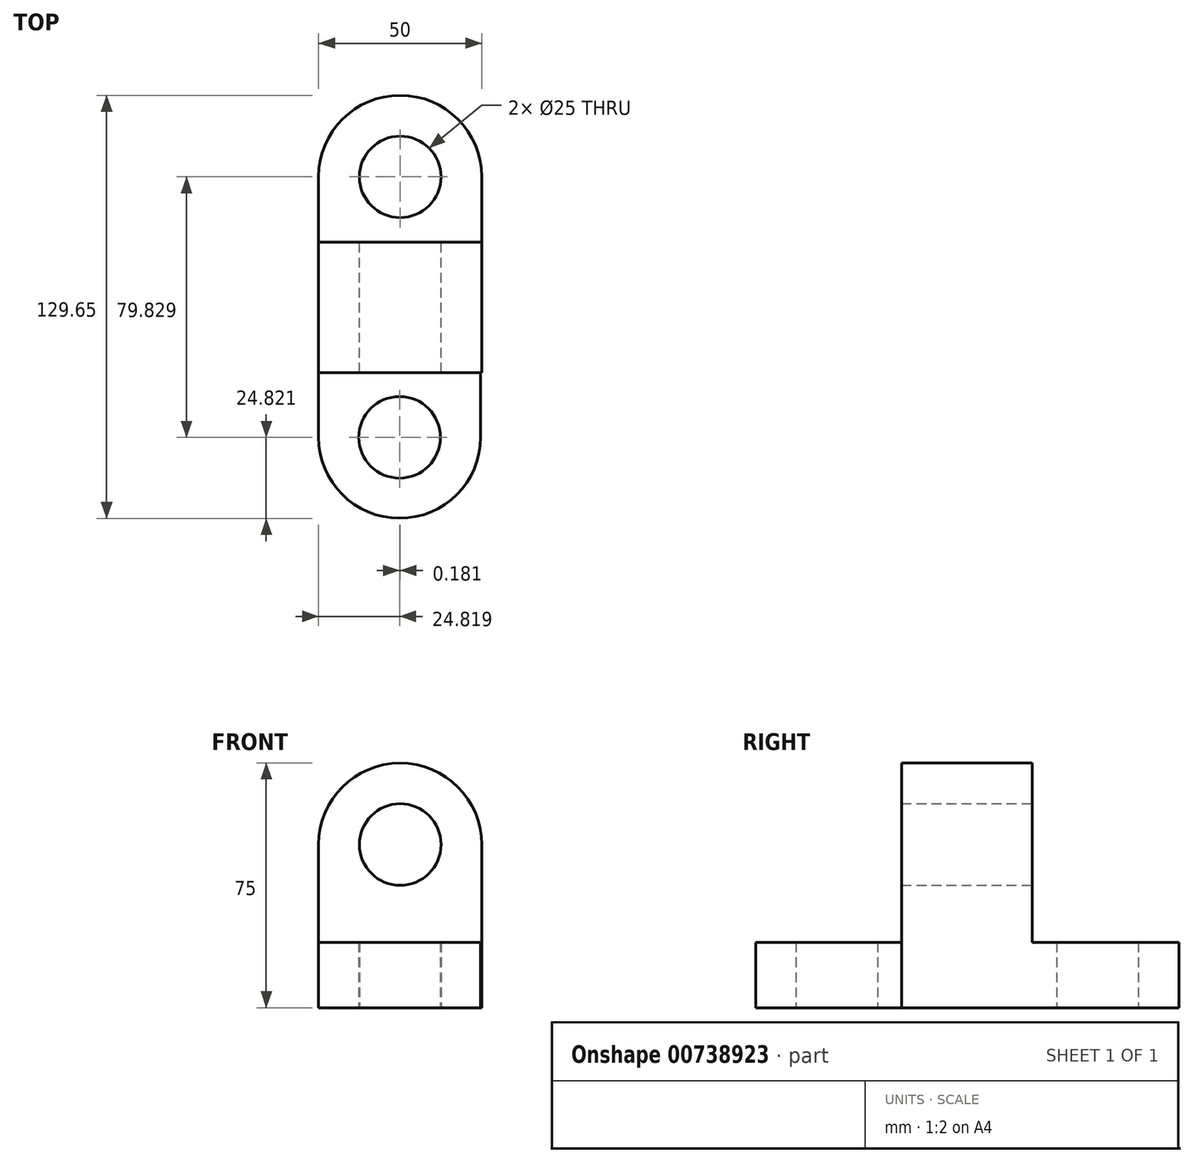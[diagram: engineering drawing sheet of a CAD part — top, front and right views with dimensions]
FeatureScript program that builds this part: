
annotation { "Feature Type Name" : "Feature", "Feature Type Description" : "" }
export const myFeature = defineFeature(function(context is Context, id is Id, definition is map)
    precondition{}
    {
        {
            var Q0;
            Q0=qCreatedBy(makeId("Front.planeOp"),FACE);
            var sketch = newSketch(context, id + "F0", { "sketchPlane" : qUnion([Q0])});
            skLineSegment(sketch, "E0.bottom", {"start": v(0, 0) * mm, "end": v(50, 0) * mm});
            skLineSegment(sketch, "E0.top", {"start": v(0, 50) * mm, "end": v(50, 50) * mm});
            skLineSegment(sketch, "E0.left", {"start": v(0, 0) * mm, "end": v(0, 50) * mm});
            skLineSegment(sketch, "E0.right", {"start": v(50, 0) * mm, "end": v(50, 50) * mm});
            skArc(sketch, "E1", {"start": v(50, 50) * mm, "mid": v(25, 75) * mm, "end": v(0, 50) * mm});
            skCircle(sketch, "E2", {"center": v(25, 50) * mm, "radius": 12.5 * mm});
            skSolve(sketch);
        }
        {
            var Q0;
            Q0 = qSketchRegion(id + "F0", true);
            extrude(context, id + "F1", {"entities" : qUnion([Q0]), "depth" : 40 * mm, "offsetDistance" : 25 * mm});
        }
        {
            var Q0;
            Q0=qCreatedBy(makeId("Top.planeOp"),FACE);
            var sketch = newSketch(context, id + "F2", { "sketchPlane" : qUnion([Q0])});
            skLineSegment(sketch, "E3.bottom", {"start": v(0, 0) * mm, "end": v(50, 0) * mm});
            skLineSegment(sketch, "E3.top", {"start": v(0, 20) * mm, "end": v(50, 20) * mm});
            skLineSegment(sketch, "E3.left", {"start": v(0, 0) * mm, "end": v(0, 20) * mm});
            skLineSegment(sketch, "E3.right", {"start": v(50, 0) * mm, "end": v(50, 20) * mm});
            skArc(sketch, "E4", {"start": v(50, 20) * mm, "mid": v(25, 45) * mm, "end": v(0, 20) * mm});
            skCircle(sketch, "E5", {"center": v(25, 20) * mm, "radius": 12.5 * mm});
            skSolve(sketch);
        }
        {
            var Q0;
            Q0 = qSketchRegion(id + "F2", true);
            extrude(context, id + "F3", {"entities" : qUnion([Q0]), "operationType" : NewBodyOperationType.ADD, "depth" : 20 * mm, "offsetDistance" : 25 * mm});
        }
        {
            var Q0;
            Q0=qCreatedBy(makeId("Top.planeOp"),FACE);
            var sketch = newSketch(context, id + "F4", { "sketchPlane" : qUnion([Q0])});
            skLineSegment(sketch, "E6", {"start": v(0, 0) * mm, "end": v(0, -39.83) * mm});
            skLineSegment(sketch, "E7.bottom", {"start": v(0, -39.83) * mm, "end": v(49.64, -39.83) * mm});
            skLineSegment(sketch, "E7.top", {"start": v(0, -59.83) * mm, "end": v(49.64, -59.83) * mm});
            skLineSegment(sketch, "E7.left", {"start": v(0, -39.83) * mm, "end": v(0, -59.83) * mm});
            skLineSegment(sketch, "E7.right", {"start": v(49.64, -39.83) * mm, "end": v(49.64, -59.83) * mm});
            skArc(sketch, "E8", {"start": v(0, -59.83) * mm, "mid": v(24.82, -84.65) * mm, "end": v(49.64, -59.83) * mm});
            skCircle(sketch, "E9", {"center": v(24.82, -59.83) * mm, "radius": 12.5 * mm});
            skSolve(sketch);
        }
        {
            var Q0;
            Q0 = qSketchRegion(id + "F4", true);
            extrude(context, id + "F5", {"entities" : qUnion([Q0]), "operationType" : NewBodyOperationType.ADD, "depth" : 20 * mm, "offsetDistance" : 25 * mm});
        }
    });
